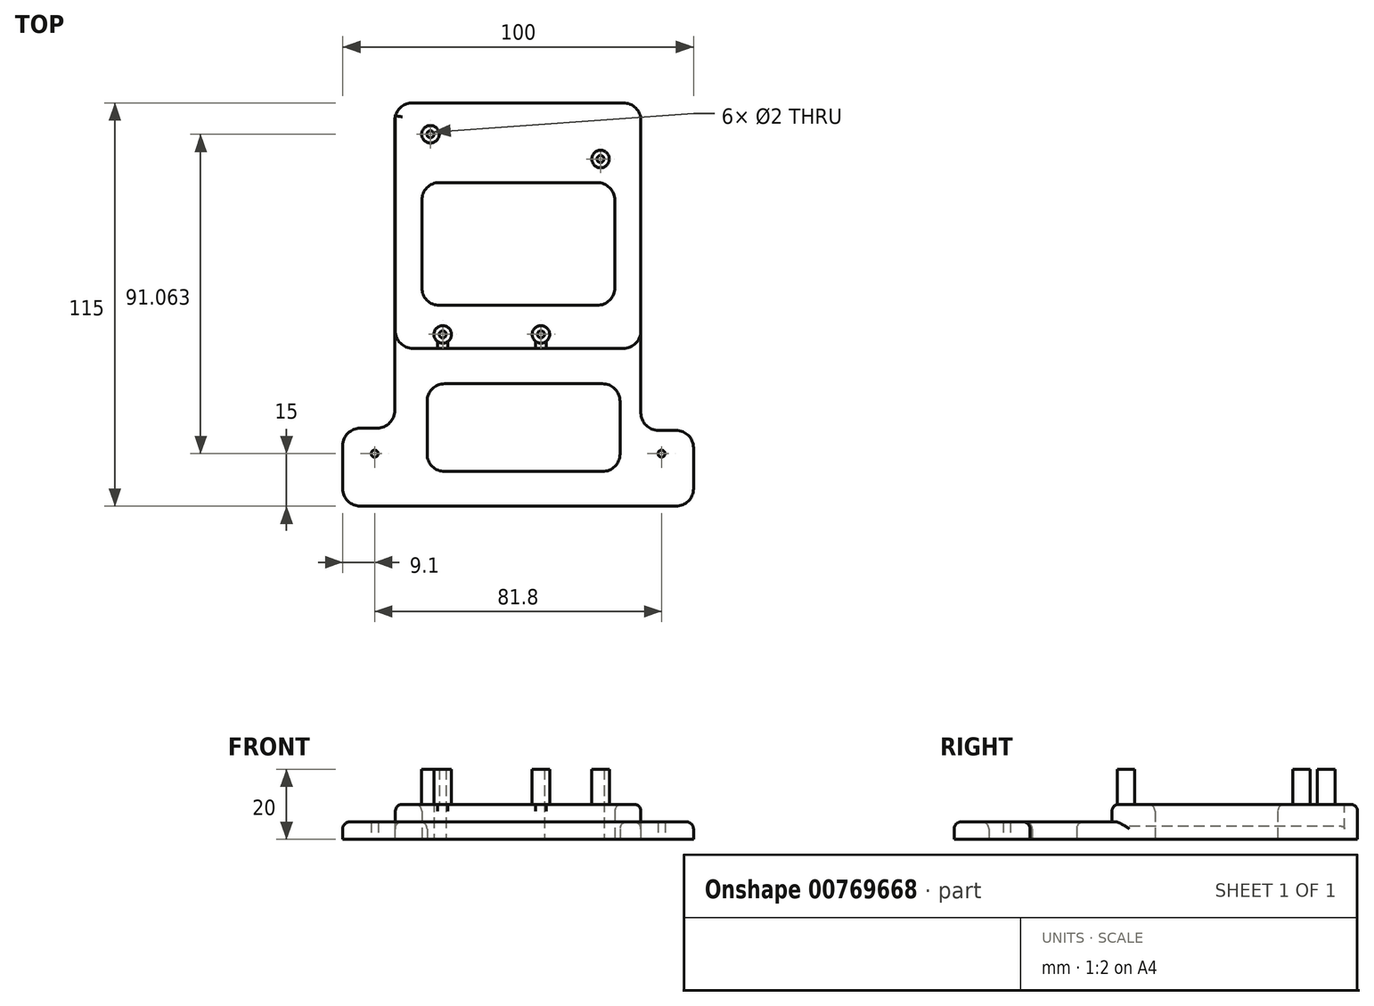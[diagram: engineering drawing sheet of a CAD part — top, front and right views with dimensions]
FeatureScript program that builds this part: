
annotation { "Feature Type Name" : "Feature", "Feature Type Description" : "" }
export const myFeature = defineFeature(function(context is Context, id is Id, definition is map)
    precondition{}
    {
        {
            var Q0;
            Q0=qCreatedBy(makeId("Top.planeOp"),FACE);
            var sketch = newSketch(context, id + "F0", { "sketchPlane" : qUnion([Q0])});
            skLineSegment(sketch, "E0.bottom", {"start": v(0, 0) * mm, "end": v(100, 0) * mm});
            skLineSegment(sketch, "E0.top", {"start": v(0, -115) * mm, "end": v(100, -115) * mm});
            skLineSegment(sketch, "E0.left", {"start": v(0, 0) * mm, "end": v(0, -115) * mm});
            skLineSegment(sketch, "E0.right", {"start": v(100, 0) * mm, "end": v(100, -115) * mm});
            skCircle(sketch, "E1", {"center": v(9.1, -100) * mm, "radius": 1 * mm});
            skCircle(sketch, "E2.1.0.0", {"center": v(90.9, -100) * mm, "radius": 1 * mm});
            skLineSegment(sketch, "E2.direction1", {"start": v(9.1, -100) * mm, "end": v(90.9, -100) * mm, "construction": true});
            skLineSegment(sketch, "E3.bottom", {"start": v(15, 0) * mm, "end": v(85, 0) * mm});
            skLineSegment(sketch, "E3.top", {"start": v(15, -70) * mm, "end": v(85, -70) * mm});
            skLineSegment(sketch, "E3.left", {"start": v(15, 0) * mm, "end": v(15, -70) * mm});
            skLineSegment(sketch, "E3.right", {"start": v(85, 0) * mm, "end": v(85, -70) * mm});
            skCircle(sketch, "E4", {"center": v(25, -8.94) * mm, "radius": 2.5 * mm});
            skCircle(sketch, "E5", {"center": v(28.5, -66) * mm, "radius": 2.5 * mm});
            skCircle(sketch, "E6.1.0.0", {"center": v(56.5, -66) * mm, "radius": 2.5 * mm});
            skLineSegment(sketch, "E6.direction1", {"start": v(28.5, -66) * mm, "end": v(56.5, -66) * mm, "construction": true});
            skCircle(sketch, "E7", {"center": v(73.5, -16) * mm, "radius": 2.5 * mm});
            skCircle(sketch, "E8", {"center": v(25, -8.94) * mm, "radius": 1 * mm});
            skCircle(sketch, "E9", {"center": v(73.5, -16) * mm, "radius": 1 * mm});
            skCircle(sketch, "E10", {"center": v(28.5, -66) * mm, "radius": 1 * mm});
            skCircle(sketch, "E11", {"center": v(56.5, -66) * mm, "radius": 1 * mm});
            skLineSegment(sketch, "E12.bottom", {"start": v(85, 0) * mm, "end": v(100, 0) * mm});
            skLineSegment(sketch, "E12.top", {"start": v(85, -93.36) * mm, "end": v(100, -93.36) * mm});
            skLineSegment(sketch, "E12.left", {"start": v(85, 0) * mm, "end": v(85, -93.36) * mm});
            skLineSegment(sketch, "E12.right", {"start": v(100, 0) * mm, "end": v(100, -93.36) * mm});
            skLineSegment(sketch, "E13.bottom", {"start": v(0, 0) * mm, "end": v(14.82, 0) * mm});
            skLineSegment(sketch, "E13.top", {"start": v(0, -92.72) * mm, "end": v(14.82, -92.72) * mm});
            skLineSegment(sketch, "E13.left", {"start": v(0, 0) * mm, "end": v(0, -92.72) * mm});
            skLineSegment(sketch, "E13.right", {"start": v(14.82, 0) * mm, "end": v(14.82, -92.72) * mm});
            skLineSegment(sketch, "E14.bottom", {"start": v(22.55, -22.73) * mm, "end": v(77.55, -22.73) * mm});
            skLineSegment(sketch, "E14.top", {"start": v(22.55, -57.73) * mm, "end": v(77.55, -57.73) * mm});
            skLineSegment(sketch, "E14.left", {"start": v(22.55, -22.73) * mm, "end": v(22.55, -57.73) * mm});
            skLineSegment(sketch, "E14.right", {"start": v(77.55, -22.73) * mm, "end": v(77.55, -57.73) * mm});
            skLineSegment(sketch, "E15.bottom", {"start": v(24.05, -80.1) * mm, "end": v(79.05, -80.1) * mm});
            skLineSegment(sketch, "E15.top", {"start": v(24.05, -105.1) * mm, "end": v(79.05, -105.1) * mm});
            skLineSegment(sketch, "E15.left", {"start": v(24.05, -80.1) * mm, "end": v(24.05, -105.1) * mm});
            skLineSegment(sketch, "E15.right", {"start": v(79.05, -80.1) * mm, "end": v(79.05, -105.1) * mm});
            skSolve(sketch);
        }
        {
            var Q0;
            {var subQ5=sQuery(id+"F0.wireOp",EDGE,"E0.top");Q0=makeQuery(id+"F0.imprint","IMPRINT",FACE,{"disambiguationData":[TD([[makeQuery(id+"F0.imprint","IMPRINT",EDGE,{"derivedFrom":subQ5}),1.0]])]});}
            extrude(context, id + "F1", {"entities" : qUnion([Q0]), "depth" : 5 * mm, "offsetDistance" : 25 * mm});
        }
        {
            var Q0;
            Q0=makeQuery(id+"F0.imprint","IMPRINT",FACE,{"disambiguationData":[TD([[makeQuery(id+"F0.imprint","IMPRINT",EDGE,{"derivedFrom":sQuery(id+"F0.wireOp",EDGE,"E3.top")}),1.0]])]});
            extrude(context, id + "F2", {"entities" : qUnion([Q0]), "operationType" : NewBodyOperationType.ADD, "depth" : 10 * mm, "offsetDistance" : 25 * mm});
        }
        {
            var Q0;
            Q0=makeQuery(id+"F0.imprint","IMPRINT",FACE,{"disambiguationData":[TD([[makeQuery(id+"F0.imprint","IMPRINT",EDGE,{"derivedFrom":sQuery(id+"F0.wireOp",EDGE,"E4")}),1.0]])]});
            var Q1;
            Q1=makeQuery(id+"F0.imprint","IMPRINT",FACE,{"disambiguationData":[TD([[makeQuery(id+"F0.imprint","IMPRINT",EDGE,{"derivedFrom":sQuery(id+"F0.wireOp",EDGE,"E7")}),1.0]])]});
            var Q2;
            Q2=makeQuery(id+"F0.imprint","IMPRINT",FACE,{"disambiguationData":[TD([[makeQuery(id+"F0.imprint","IMPRINT",EDGE,{"derivedFrom":sQuery(id+"F0.wireOp",EDGE,"E6.1.0.0")}),1.0]])]});
            var Q3;
            Q3=makeQuery(id+"F0.imprint","IMPRINT",FACE,{"disambiguationData":[TD([[makeQuery(id+"F0.imprint","IMPRINT",EDGE,{"derivedFrom":sQuery(id+"F0.wireOp",EDGE,"E5")}),1.0]])]});
            extrude(context, id + "F3", {"entities" : qUnion([Q0, Q1, Q2, Q3]), "operationType" : NewBodyOperationType.ADD, "depth" : 20 * mm, "offsetDistance" : 25 * mm});
        }
        {
            var Q0;
            Q0=makeQuery(id+"F2.opExtrude","SWEPT_EDGE",EDGE,{"disambiguationData":[OSD([sQuery(id+"F0.wireOp",EDGE,"E14.bottom"),sQuery(id+"F0.wireOp",EDGE,"E14.left")])]});
            var Q1;
            Q1=makeQuery(id+"F2.opExtrude","SWEPT_EDGE",EDGE,{"disambiguationData":[OSD([sQuery(id+"F0.wireOp",EDGE,"E14.bottom"),sQuery(id+"F0.wireOp",EDGE,"E14.right")])]});
            var Q2;
            Q2=makeQuery(id+"F2.opExtrude","SWEPT_EDGE",EDGE,{"disambiguationData":[OSD([sQuery(id+"F0.wireOp",EDGE,"E14.top"),sQuery(id+"F0.wireOp",EDGE,"E14.right")])]});
            var Q3;
            Q3=makeQuery(id+"F2.opExtrude","SWEPT_EDGE",EDGE,{"disambiguationData":[OSD([sQuery(id+"F0.wireOp",EDGE,"E14.top"),sQuery(id+"F0.wireOp",EDGE,"E14.left")])]});
            var Q4;
            Q4=makeQuery(id+"F1.opExtrude","SWEPT_EDGE",EDGE,{"disambiguationData":[OSD([sQuery(id+"F0.wireOp",EDGE,"E15.bottom"),sQuery(id+"F0.wireOp",EDGE,"E15.left")])]});
            var Q5;
            Q5=makeQuery(id+"F1.opExtrude","SWEPT_EDGE",EDGE,{"disambiguationData":[OSD([sQuery(id+"F0.wireOp",EDGE,"E15.top"),sQuery(id+"F0.wireOp",EDGE,"E15.left")])]});
            var Q6;
            Q6=makeQuery(id+"F1.opExtrude","SWEPT_EDGE",EDGE,{"disambiguationData":[OSD([sQuery(id+"F0.wireOp",EDGE,"E15.top"),sQuery(id+"F0.wireOp",EDGE,"E15.right")])]});
            var Q7;
            Q7=makeQuery(id+"F1.opExtrude","SWEPT_EDGE",EDGE,{"disambiguationData":[OSD([sQuery(id+"F0.wireOp",EDGE,"E15.bottom"),sQuery(id+"F0.wireOp",EDGE,"E15.right")])]});
            var Q8;
            Q8=makeQuery(id+"F1.opExtrude","SWEPT_EDGE",EDGE,{"disambiguationData":[OSD([sQuery(id+"F0.wireOp",EDGE,"E12.top"),sQuery(id+"F0.wireOp",EDGE,"E12.left")])]});
            var Q9;
            Q9=makeQuery(id+"F1.opExtrude","SWEPT_EDGE",EDGE,{"disambiguationData":[OSD([sQuery(id+"F0.wireOp",EDGE,"E0.right"),sQuery(id+"F0.wireOp",EDGE,"E12.top")])]});
            var Q10;
            Q10=makeQuery(id+"F1.opExtrude","SWEPT_EDGE",EDGE,{"disambiguationData":[OSD([sQuery(id+"F0.wireOp",EDGE,"E0.top"),sQuery(id+"F0.wireOp",EDGE,"E0.right")])]});
            var Q11;
            Q11=makeQuery(id+"F1.opExtrude","SWEPT_EDGE",EDGE,{"disambiguationData":[OSD([sQuery(id+"F0.wireOp",EDGE,"E0.top"),sQuery(id+"F0.wireOp",EDGE,"E0.left")])]});
            var Q12;
            Q12=makeQuery(id+"F1.opExtrude","SWEPT_EDGE",EDGE,{"disambiguationData":[OSD([sQuery(id+"F0.wireOp",EDGE,"E0.left"),sQuery(id+"F0.wireOp",EDGE,"E13.top")])]});
            var Q13;
            Q13=makeQuery(id+"F1.opExtrude","SWEPT_EDGE",EDGE,{"disambiguationData":[OSD([sQuery(id+"F0.wireOp",EDGE,"E13.top"),sQuery(id+"F0.wireOp",EDGE,"E13.right")])]});
            var Q14;
            Q14=makeQuery(id+"F2.opExtrude","SWEPT_EDGE",EDGE,{"disambiguationData":[OSD([sQuery(id+"F0.wireOp",EDGE,"E3.top"),sQuery(id+"F0.wireOp",EDGE,"E3.right"),sQuery(id+"F0.wireOp",EDGE,"E12.left")])]});
            var Q15;
            Q15=makeQuery(id+"F2.opExtrude","SWEPT_EDGE",EDGE,{"disambiguationData":[OSD([sQuery(id+"F0.wireOp",EDGE,"E3.top"),sQuery(id+"F0.wireOp",EDGE,"E3.left")])]});
            var Q16;
            Q16=makeQuery(id+"F1.opExtrude","SWEPT_EDGE",EDGE,{"disambiguationData":[OSD([sQuery(id+"F0.wireOp",EDGE,"E0.bottom"),sQuery(id+"F0.wireOp",EDGE,"E13.right")])]});
            var Q17;
            Q17=makeQuery(id+"F2.opExtrude","SWEPT_EDGE",EDGE,{"disambiguationData":[OSD([sQuery(id+"F0.wireOp",EDGE,"E0.bottom"),sQuery(id+"F0.wireOp",EDGE,"E3.right")])]});
            fillet(context, id + "F4", {"entities" : qUnion([Q0, Q1, Q2, Q3, Q4, Q5, Q6, Q7, Q8, Q9, Q10, Q11, Q12, Q13, Q14, Q15, Q16, Q17]), "radius" : 5 * mm, "tangentPropagation" : true, "allowEdgeOverflow" : false});
        }
        {
            var Q0;
            Q0=makeQuery(id+"F2.opExtrude","CAP_EDGE",EDGE,{"disambiguationData":[OSD([sQuery(id+"F0.wireOp",EDGE,"E3.top")])],"isStart":false});
            var Q1;
            Q1=makeQuery(id+"F1.opExtrude","CAP_EDGE",EDGE,{"disambiguationData":[OSD([sQuery(id+"F0.wireOp",EDGE,"E0.top")])],"isStart":false});
            var Q2;
            Q2=makeQuery(id+"F1.opExtrude","CAP_EDGE",EDGE,{"disambiguationData":[OSD([sQuery(id+"F0.wireOp",EDGE,"E15.bottom")])],"isStart":false});
            var Q3;
            Q3=makeQuery(id+"F2.opExtrude","CAP_EDGE",EDGE,{"disambiguationData":[OSD([sQuery(id+"F0.wireOp",EDGE,"E14.bottom")])],"isStart":false});
            fillet(context, id + "F5", {"entities" : qUnion([Q0, Q1, Q2, Q3]), "radius" : 2 * mm, "tangentPropagation" : true, "allowEdgeOverflow" : false});
        }
    });
